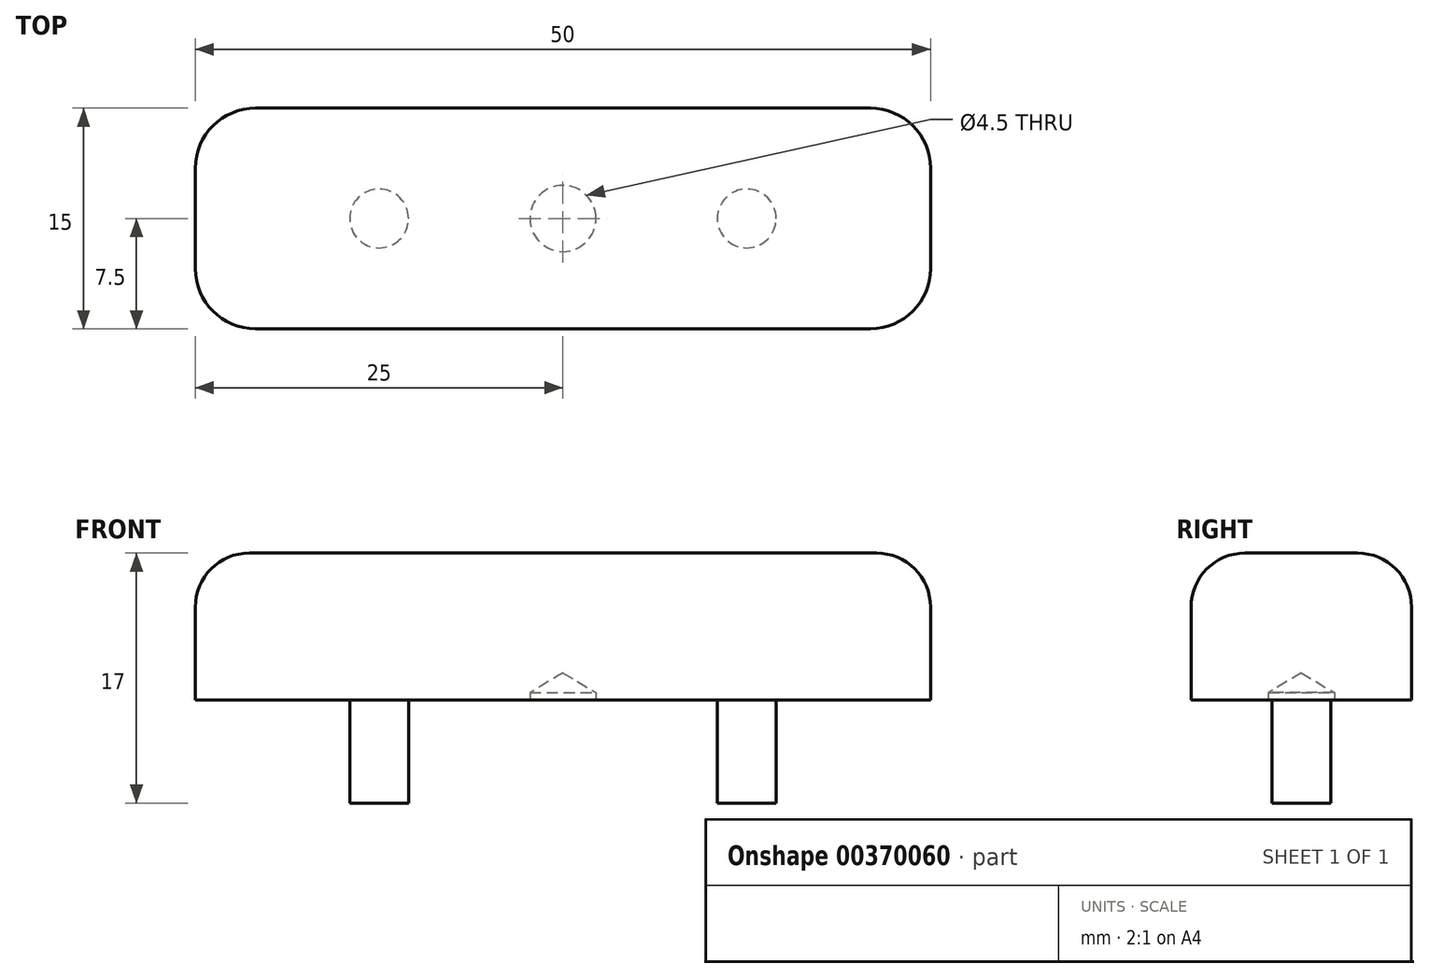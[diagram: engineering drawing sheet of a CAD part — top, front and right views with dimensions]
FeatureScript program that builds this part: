
annotation { "Feature Type Name" : "Feature", "Feature Type Description" : "" }
export const myFeature = defineFeature(function(context is Context, id is Id, definition is map)
    precondition{}
    {
        {
            var Q0;
            Q0=qCreatedBy(makeId("Top.planeOp"),FACE);
            var sketch = newSketch(context, id + "F0", { "sketchPlane" : qUnion([Q0])});
            skLineSegment(sketch, "E0.bottom", {"start": v(25, 7.5) * mm, "end": v(-25, 7.5) * mm});
            skLineSegment(sketch, "E0.top", {"start": v(25, -7.5) * mm, "end": v(-25, -7.5) * mm});
            skLineSegment(sketch, "E0.left", {"start": v(25, 7.5) * mm, "end": v(25, -7.5) * mm});
            skLineSegment(sketch, "E0.right", {"start": v(-25, 7.5) * mm, "end": v(-25, -7.5) * mm});
            skPoint(sketch, "E0.middle", {"position": v(0, 0) * mm});
            skPoint(sketch, "E1", {"position": v(-12.5, 0) * mm});
            skPoint(sketch, "E2", {"position": v(12.5, 0) * mm});
            skCircle(sketch, "E3", {"center": v(-12.5, 0) * mm, "radius": 2 * mm});
            skCircle(sketch, "E4", {"center": v(12.5, 0) * mm, "radius": 2 * mm});
            skSolve(sketch);
        }
        {
            var Q0;
            Q0=makeQuery(id+"F0.imprint","IMPRINT",FACE,{"disambiguationData":[TD([[makeQuery(id+"F0.imprint","IMPRINT",EDGE,{"derivedFrom":sQuery(id+"F0.wireOp",EDGE,"E0.bottom")}),1.0]])]});
            var Q1;
            Q1=makeQuery(id+"F0.imprint","IMPRINT",FACE,{"disambiguationData":[TD([[makeQuery(id+"F0.imprint","IMPRINT",EDGE,{"derivedFrom":sQuery(id+"F0.wireOp",EDGE,"E4")}),1.0]])]});
            var Q2;
            Q2=makeQuery(id+"F0.imprint","IMPRINT",FACE,{"disambiguationData":[TD([[makeQuery(id+"F0.imprint","IMPRINT",EDGE,{"derivedFrom":sQuery(id+"F0.wireOp",EDGE,"E3")}),1.0]])]});
            extrude(context, id + "F1", {"entities" : qUnion([Q0, Q1, Q2]), "depth" : 10 * mm, "offsetDistance" : 25.4 * mm});
        }
        {
            var Q0;
            Q0=makeQuery(id+"F1.opExtrude","CAP_EDGE",EDGE,{"disambiguationData":[OSD([sQuery(id+"F0.wireOp",EDGE,"E0.top")])],"isStart":false});
            var Q1;
            Q1=makeQuery(id+"F1.opExtrude","CAP_EDGE",EDGE,{"disambiguationData":[OSD([sQuery(id+"F0.wireOp",EDGE,"E0.right")])],"isStart":false});
            var Q2;
            Q2=makeQuery(id+"F1.opExtrude","CAP_EDGE",EDGE,{"disambiguationData":[OSD([sQuery(id+"F0.wireOp",EDGE,"E0.left")])],"isStart":false});
            var Q3;
            Q3=makeQuery(id+"F1.opExtrude","CAP_EDGE",EDGE,{"disambiguationData":[OSD([sQuery(id+"F0.wireOp",EDGE,"E0.bottom")])],"isStart":false});
            fillet(context, id + "F2", {"entities" : qUnion([Q0, Q1, Q2, Q3]), "radius" : 3.68 * mm, "tangentPropagation" : true, "allowEdgeOverflow" : false});
        }
        {
            var Q0;
            Q0=makeQuery(id+"F2.opFillet","BLEND_EDGE",EDGE,{"blendedFrom":[makeQuery(id+"F1.opExtrude","CAP_EDGE",EDGE,{"disambiguationData":[OSD([sQuery(id+"F0.wireOp",EDGE,"E0.top")])],"isStart":false}),makeQuery(id+"F1.opExtrude","CAP_EDGE",EDGE,{"disambiguationData":[OSD([sQuery(id+"F0.wireOp",EDGE,"E0.left")])],"isStart":false})],"blendedInto":[]});
            var Q1;
            Q1=makeQuery(id+"F2.opFillet","BLEND_EDGE",EDGE,{"blendedFrom":[makeQuery(id+"F1.opExtrude","CAP_EDGE",EDGE,{"disambiguationData":[OSD([sQuery(id+"F0.wireOp",EDGE,"E0.bottom")])],"isStart":false}),makeQuery(id+"F1.opExtrude","CAP_EDGE",EDGE,{"disambiguationData":[OSD([sQuery(id+"F0.wireOp",EDGE,"E0.left")])],"isStart":false})],"blendedInto":[]});
            var Q2;
            Q2=makeQuery(id+"F2.opFillet","BLEND_EDGE",EDGE,{"blendedFrom":[makeQuery(id+"F1.opExtrude","CAP_EDGE",EDGE,{"disambiguationData":[OSD([sQuery(id+"F0.wireOp",EDGE,"E0.top")])],"isStart":false}),makeQuery(id+"F1.opExtrude","CAP_EDGE",EDGE,{"disambiguationData":[OSD([sQuery(id+"F0.wireOp",EDGE,"E0.right")])],"isStart":false})],"blendedInto":[]});
            var Q3;
            Q3=makeQuery(id+"F2.opFillet","BLEND_EDGE",EDGE,{"blendedFrom":[makeQuery(id+"F1.opExtrude","CAP_EDGE",EDGE,{"disambiguationData":[OSD([sQuery(id+"F0.wireOp",EDGE,"E0.bottom")])],"isStart":false}),makeQuery(id+"F1.opExtrude","CAP_EDGE",EDGE,{"disambiguationData":[OSD([sQuery(id+"F0.wireOp",EDGE,"E0.right")])],"isStart":false})],"blendedInto":[]});
            fillet(context, id + "F3", {"entities" : qUnion([Q0, Q1, Q2, Q3]), "radius" : 4.1 * mm, "tangentPropagation" : true, "allowEdgeOverflow" : false});
        }
        {
            var Q0;
            Q0=sQuery(id+"F0.wireOp",VERTEX,"E0.middle");
            var Q1;
            Q1=makeQuery(id+"F1.opExtrude","SWEPT_BODY",BODY,{"disambiguationData":[OSD([sQuery(id+"F0.wireOp",EDGE,"E0.bottom"),sQuery(id+"F0.wireOp",EDGE,"E0.top"),sQuery(id+"F0.wireOp",EDGE,"E0.left"),sQuery(id+"F0.wireOp",EDGE,"E0.right")])]});
            hole(context, id + "F4", {"style" : HoleStyle.SIMPLE, "endStyle" : HoleEndStyle.BLIND, "oppositeDirection" : true, "holeDiameter" : 4.5 * mm, "majorDiameter" : 6.35 * mm, "holeDepth" : 0.5 * mm, "isTappedThrough" : true, "tappedDepth" : 12.7 * mm, "tapClearance" : 3, "locations" : qUnion([Q0]), "scope" : qUnion([Q1])});
        }
        {
            var Q0;
            Q0=makeQuery(id+"F0.imprint","IMPRINT",FACE,{"disambiguationData":[TD([[makeQuery(id+"F0.imprint","IMPRINT",EDGE,{"derivedFrom":sQuery(id+"F0.wireOp",EDGE,"E4")}),1.0]])]});
            var Q1;
            Q1=makeQuery(id+"F0.imprint","IMPRINT",FACE,{"disambiguationData":[TD([[makeQuery(id+"F0.imprint","IMPRINT",EDGE,{"derivedFrom":sQuery(id+"F0.wireOp",EDGE,"E3")}),1.0]])]});
            extrude(context, id + "F5", {"entities" : qUnion([Q0, Q1]), "operationType" : NewBodyOperationType.ADD, "oppositeDirection" : true, "depth" : 7 * mm, "offsetDistance" : 25.4 * mm});
        }
    });
